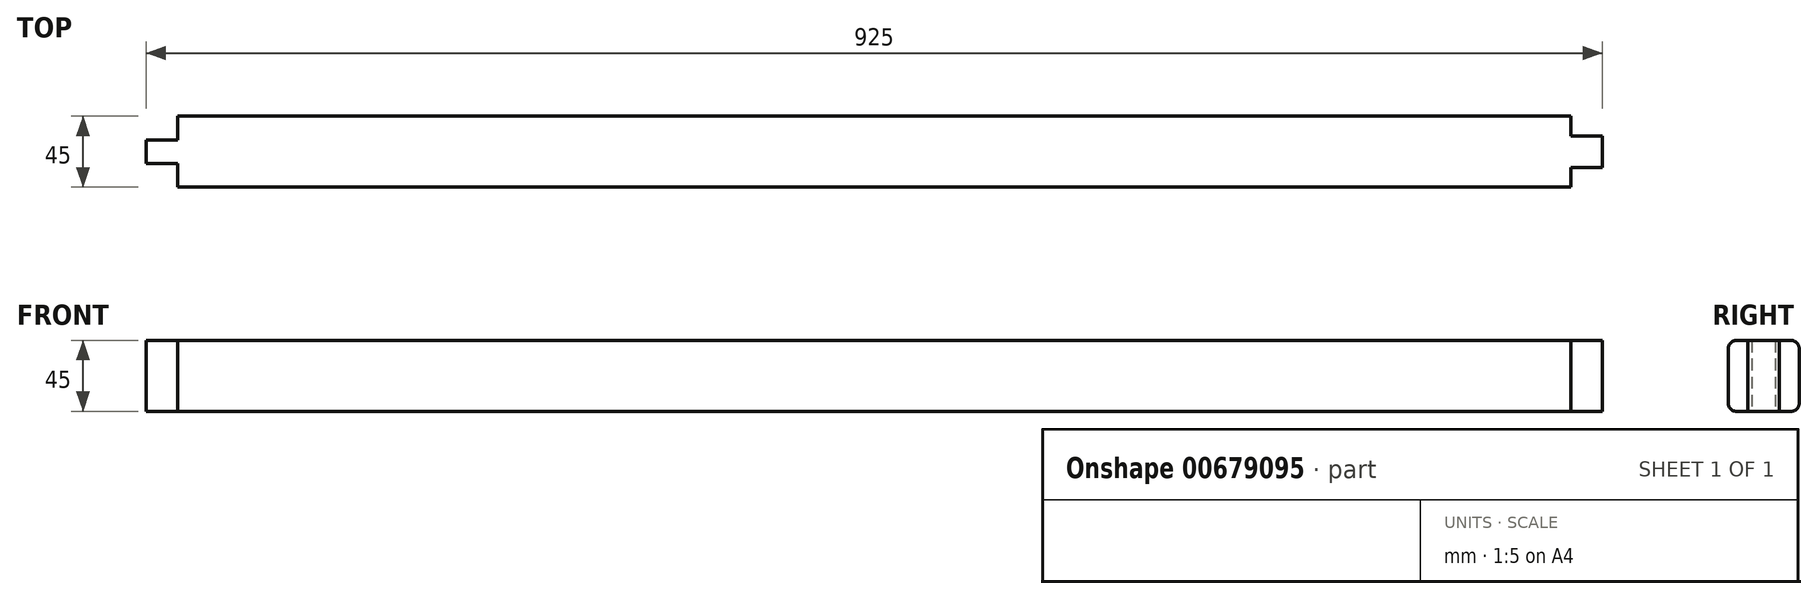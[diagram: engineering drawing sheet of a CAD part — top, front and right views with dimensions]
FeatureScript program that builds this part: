
annotation { "Feature Type Name" : "Feature", "Feature Type Description" : "" }
export const myFeature = defineFeature(function(context is Context, id is Id, definition is map)
    precondition{}
    {
        {
            var Q0;
            Q0=qCreatedBy(makeId("Right.planeOp"),FACE);
            var sketch = newSketch(context, id + "F0", { "sketchPlane" : qUnion([Q0])});
            skLineSegment(sketch, "E0.bottom", {"start": v(22.5, 22.5) * mm, "end": v(-22.5, 22.5) * mm});
            skLineSegment(sketch, "E0.top", {"start": v(22.5, -22.5) * mm, "end": v(-22.5, -22.5) * mm});
            skLineSegment(sketch, "E0.left", {"start": v(22.5, 22.5) * mm, "end": v(22.5, -22.5) * mm});
            skLineSegment(sketch, "E0.right", {"start": v(-22.5, 22.5) * mm, "end": v(-22.5, -22.5) * mm});
            skPoint(sketch, "E0.middle", {"position": v(0, 0) * mm});
            skSolve(sketch);
        }
        {
            var Q0;
            Q0 = qSketchRegion(id + "F0", true);
            extrude(context, id + "F1", {"entities" : qUnion([Q0]), "endBound" : BoundingType.SYMMETRIC, "depth" : 885 * mm, "offsetDistance" : 25 * mm});
        }
        {
            var Q0;
            Q0=makeQuery(id+"F1.opExtrude","CAP_FACE",FACE,{"disambiguationData":[OSD([sQuery(id+"F0.wireOp",EDGE,"E0.bottom"),sQuery(id+"F0.wireOp",EDGE,"E0.top"),sQuery(id+"F0.wireOp",EDGE,"E0.left"),sQuery(id+"F0.wireOp",EDGE,"E0.right")])],"isStart":false});
            var sketch = newSketch(context, id + "F2", { "sketchPlane" : qUnion([Q0])});
            skLineSegment(sketch, "E1.bottom", {"start": v(10, 22.5) * mm, "end": v(-10, 22.5) * mm});
            skLineSegment(sketch, "E1.top", {"start": v(10, -22.5) * mm, "end": v(-10, -22.5) * mm});
            skLineSegment(sketch, "E1.left", {"start": v(10, 22.5) * mm, "end": v(10, -22.5) * mm});
            skLineSegment(sketch, "E1.right", {"start": v(-10, 22.5) * mm, "end": v(-10, -22.5) * mm});
            skPoint(sketch, "E1.middle", {"position": v(0, 0) * mm});
            skSolve(sketch);
        }
        {
            var Q0;
            Q0 = qSketchRegion(id + "F2", true);
            extrude(context, id + "F3", {"entities" : qUnion([Q0]), "operationType" : NewBodyOperationType.ADD, "depth" : 20 * mm, "offsetDistance" : 25 * mm});
        }
        {
            var Q0;
            Q0=makeQuery(id+"F1.opExtrude","CAP_FACE",FACE,{"disambiguationData":[OSD([sQuery(id+"F0.wireOp",EDGE,"E0.bottom"),sQuery(id+"F0.wireOp",EDGE,"E0.top"),sQuery(id+"F0.wireOp",EDGE,"E0.left"),sQuery(id+"F0.wireOp",EDGE,"E0.right")])],"isStart":true});
            var sketch = newSketch(context, id + "F4", { "sketchPlane" : qUnion([Q0])});
            skLineSegment(sketch, "E2.bottom", {"start": v(7.5, 22.5) * mm, "end": v(-7.5, 22.5) * mm});
            skLineSegment(sketch, "E2.top", {"start": v(7.5, -22.5) * mm, "end": v(-7.5, -22.5) * mm});
            skLineSegment(sketch, "E2.left", {"start": v(7.5, 22.5) * mm, "end": v(7.5, -22.5) * mm});
            skLineSegment(sketch, "E2.right", {"start": v(-7.5, 22.5) * mm, "end": v(-7.5, -22.5) * mm});
            skPoint(sketch, "E2.middle", {"position": v(0, 0) * mm});
            skSolve(sketch);
        }
        {
            var Q0;
            Q0 = qSketchRegion(id + "F4", true);
            extrude(context, id + "F5", {"entities" : qUnion([Q0]), "operationType" : NewBodyOperationType.ADD, "depth" : 20 * mm, "offsetDistance" : 25 * mm});
        }
        {
            var Q0;
            Q0=makeQuery(id+"F1.opExtrude","SWEPT_EDGE",EDGE,{"disambiguationData":[OSD([sQuery(id+"F0.wireOp",EDGE,"E0.bottom"),sQuery(id+"F0.wireOp",EDGE,"E0.right")])]});
            var Q1;
            Q1=makeQuery(id+"F1.opExtrude","SWEPT_EDGE",EDGE,{"disambiguationData":[OSD([sQuery(id+"F0.wireOp",EDGE,"E0.bottom"),sQuery(id+"F0.wireOp",EDGE,"E0.left")])]});
            var Q2;
            Q2=makeQuery(id+"F1.opExtrude","SWEPT_EDGE",EDGE,{"disambiguationData":[OSD([sQuery(id+"F0.wireOp",EDGE,"E0.top"),sQuery(id+"F0.wireOp",EDGE,"E0.right")])]});
            var Q3;
            Q3=makeQuery(id+"F1.opExtrude","SWEPT_EDGE",EDGE,{"disambiguationData":[OSD([sQuery(id+"F0.wireOp",EDGE,"E0.top"),sQuery(id+"F0.wireOp",EDGE,"E0.left")])]});
            fillet(context, id + "F6", {"entities" : qUnion([Q0, Q1, Q2, Q3]), "radius" : 5 * mm, "tangentPropagation" : true, "allowEdgeOverflow" : false});
        }
    });
